# Revit family: LAMP_KOMBIC 150 ROUND IP40 CRI80 OPAL
name_source: partatom
category: Luminarias
revit_build: Autodesk Revit 2018 (Build: 20190510_1515(x64)
units: mm (PartAtom-declared; Revit-internal decimal feet)

## family parameters
Anfitrión = Cara
Compartido = No
Corte con vacíos al cargar = No
Cota de conector redondo = Diámetro de uso
Origen de luz = Sí
Punto de cálculo de habitación = No
Tipo de pieza = Normal

## types (18) — shared parameters
CRI = 80
Cambio de temperatura de color de luz atenuada = <Ninguno>
Diameter = 150 mm
Elevación por defecto = 1219 mm
Fabricante = LAMP
Filtro de color = 16777215
Gear = Electronic
Height = 100 mm  [stored 0.328084 ft]
IEE = A+
Installation instructions = https://www.lamp.es
Insulation class = II
Lamp = COB LED
Last update = 26/08/2021
Luminaire type = Downlight
MacAdam = 3
Manufacturer URL = http://www.lamp.es
Manufacturer country = Spain
Manufacturer name = LAMP
Material aro = LAMP_Plástico genérico BL
Material difusor = LAMP_PMMA Difusor Kombic
Material disipador = LAMP_Aluminio Disipador Kombic
Power Supply = 220-240V 50/60Hz
Product URL = https://www.lamp.es
Product datasheet = http://www.lamp.es
Protection rating = IP40
Recessed diameter = 145 mm  [stored 0.475722 ft]
Type = COB PHILIPS
Weight = 0.70 kg
Ángulo de inclinación = -90.00°

## per-type parameters (varying)
| type | Archivo de red fotométrica | Efficacy | Finish | LED Lifetime | Material reflector | Modelo | Plum | Power | Product code |
| 1427LM 3000K  M/W | K21RD2040OP830NMW.IES | 104 lm/W | Shiny white RAL 9010 | 50.000 L90 B10 | LAMP_PC Reflector Kombic Metalizado Mate | K21RD2040OP830NMW | 14 W | 12 W | K21RD2040OP830NMW |
| 1473LM 3000K  W/W | K21RD2040OP830NWW.IES | 108 lm/W | Matte white RAL 9010 | 50.000 L90 B10 | LAMP_PC Reflector Kombic Blanco | K21RD2040OP830NWW | 14 W | 12 W | K21RD2040OP830NWW |
| 1486LM 4000K  M/W | K21RD2040OP840NMW.IES | 109 lm/W | Shiny white RAL 9010 | 50.000 L90 B10 | LAMP_PC Reflector Kombic Metalizado Mate | K21RD2040OP840NMW | 14 W | 12 W | K21RD2040OP840NMW |
| 1488LM 3000K  BR/W | K21RD2040OP830NRW.IES | 111 lm/W | Shiny white RAL 9010 | 50.000 L90 B10 | LAMP_PC Reflector Kombic Metalizado Brillante | K21RD2040OP830NRW | 14 W | 12 W | K21RD2040OP830NRW |
| 1534LM 4000K  W/W | K21RD2040OP840NWW.IES | 112 lm/W | Matte white RAL 9010 | 50.000 L90 B10 | LAMP_PC Reflector Kombic Blanco | K21RD2040OP840NWW | 14 W | 12 W | K21RD2040OP840NWW |
| 1550LM 4000K  BR/W | K21RD2040OP840NRW.IES | 113 lm/W | Shiny white RAL 9010 | 50.000 L90 B10 | LAMP_PC Reflector Kombic Metalizado Brillante | K21RD2040OP840NRW | 14 W | 12 W | K21RD2040OP840NRW |
| 2010LM 3000K  M/W | K21RD3040OP830NMW.IES | 101 lm/W | Shiny white RAL 9010 | 50.000 L70 B10 | LAMP_PC Reflector Kombic Metalizado Mate | K21RD3040OP830NMW | 20 W | 18 W | K21RD3040OP830NMW |
| 2074LM 3000K  W/W | K21RD3040OP830NWW.IES | 104 lm/W | Matte white RAL 9010 | 50.000 L70 B10 | LAMP_PC Reflector Kombic Blanco | K21RD3040OP830NWW | 20 W | 18 W | K21RD3040OP830NWW |
| 2094LM 4000K  M/W | K21RD3040OP840NMW.IES | 105 lm/W | Shiny white RAL 9010 | 50.000 L70 B10 | LAMP_PC Reflector Kombic Metalizado Mate | K21RD3040OP840NMW | 20 W | 18 W | K21RD3040OP840NMW |
| 2096LM 3000K  BR/W | K21RD3040OP830NRW.IES | 105 lm/W | Shiny white RAL 9010 | 50.000 L70 B10 | LAMP_PC Reflector Kombic Metalizado Brillante | K21RD3040OP830NRW | 20 W | 18 W | K21RD3040OP830NRW |
| 2161LM 4000K  W/W | K21RD3040OP840NWW.IES | 109 lm/W | Matte white RAL 9010 | 50.000 L70 B10 | LAMP_PC Reflector Kombic Blanco | K21RD3040OP840NWW | 20 W | 18 W | K21RD3040OP840NWW |
| 2184LM 4000K  BR/W | K21RD3040OP840NRW.IES | 110 lm/W | Shiny white RAL 9010 | 50.000 L70 B10 | LAMP_PC Reflector Kombic Metalizado Brillante | K21RD3040OP840NRW | 20 W | 18 W | K21RD3040OP840NRW |
| 2673LM 3000K  M/W | K21RD3540OP830NMW.IES | 97 lm/W | Shiny white RAL 9010 | 50.000 L70 B10 | LAMP_PC Reflector Kombic Metalizado Mate | K21RD3540OP830NMW | 28 W | 25 W | K21RD3540OP830NMW |
| 2759LM 3000K  W/W | K21RD3540OP830NWW.IES | 97 lm/W | Matte white RAL 9010 | 50.000 L70 B10 | LAMP_PC Reflector Kombic Blanco | K21RD3540OP830NWW | 28 W | 25 W | K21RD3540OP830NWW |
| 2784LM 4000K  M/W | K21RD3540OP840NMW.IES | 101 lm/W | Shiny white RAL 9010 | 50.000 L70 B10 | LAMP_PC Reflector Kombic Metalizado Mate | K21RD3540OP840NMW | 28 W | 25 W | K21RD3540OP840NMW |
| 2788LM 3000K  BR/W | K21RD3540OP830NRW.IES | 101 lm/W | Shiny white RAL 9010 | 50.000 L70 B10 | LAMP_PC Reflector Kombic Metalizado Brillante | K21RD3540OP830NRW | 28 W | 25 W | K21RD3540OP830NRW |
| 2874LM 4000K  W/W | K21RD3540OP840NWW.IES | 104 lm/W | Matte white RAL 9010 | 50.000 L70 B10 | LAMP_PC Reflector Kombic Blanco | K21RD3540OP840NWW | 28 W | 25 W | K21RD3540OP840NWW |
| 2904LM 4000K  BR/W | K21RD3540OP840NRW.IES | 105 lm/W | Shiny white RAL 9010 | 50.000 L70 B10 | LAMP_PC Reflector Kombic Metalizado Brillante | K21RD3540OP840NRW | 28 W | 25 W | K21RD3540OP840NRW |

note: [stored X ft] marks values corroborated as IEEE doubles in the binary element streams (Revit-internal decimal feet)
